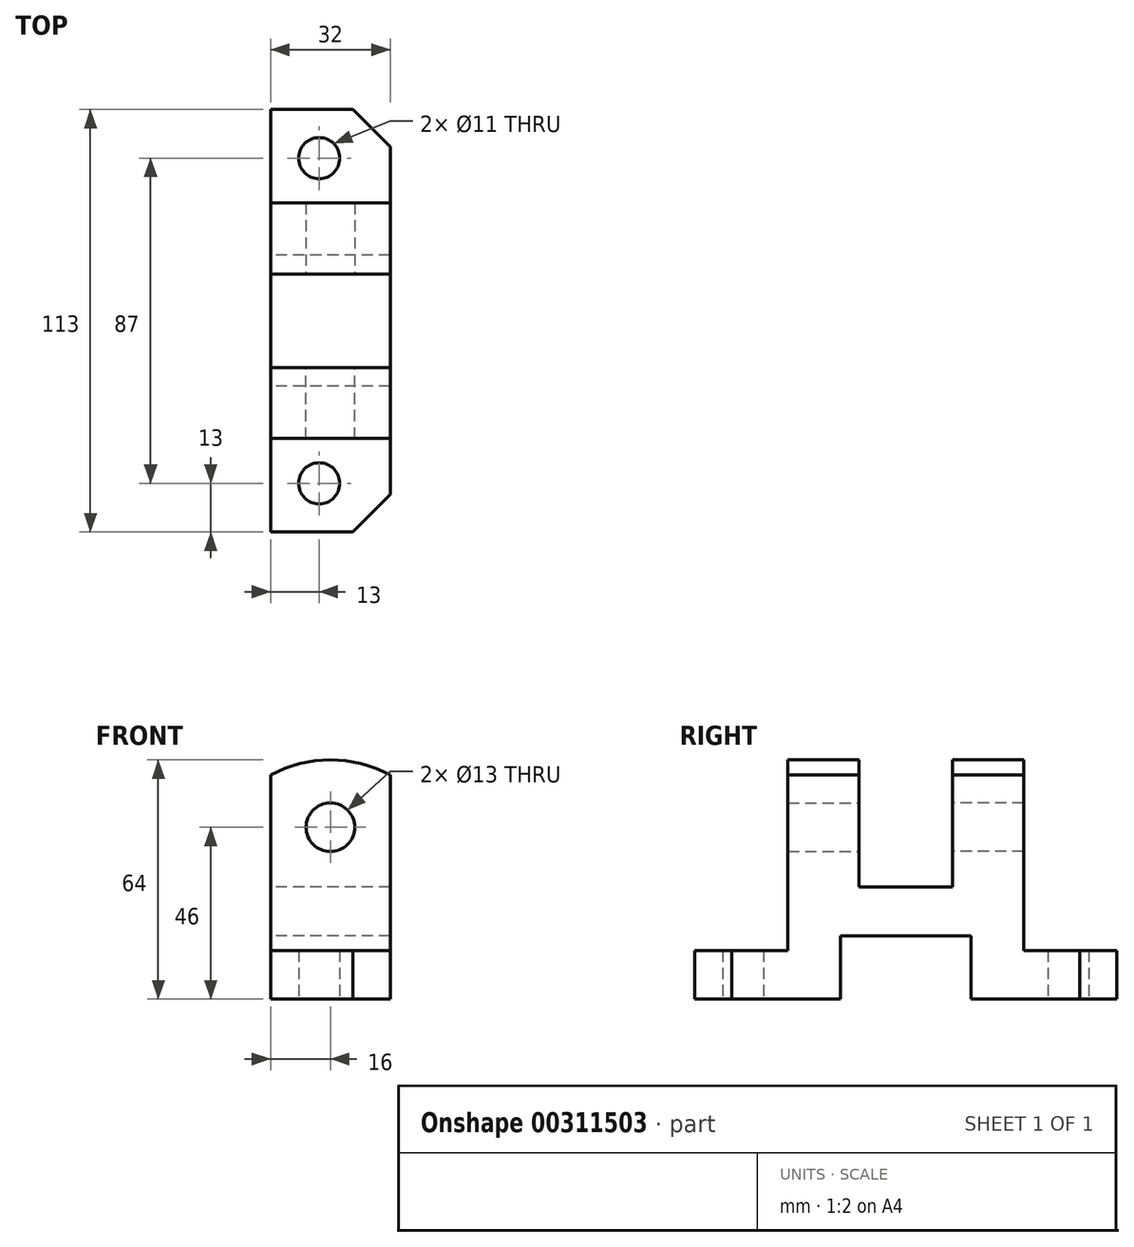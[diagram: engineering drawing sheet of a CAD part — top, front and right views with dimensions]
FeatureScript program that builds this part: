
annotation { "Feature Type Name" : "Feature", "Feature Type Description" : "" }
export const myFeature = defineFeature(function(context is Context, id is Id, definition is map)
    precondition{}
    {
        {
            var Q0;
            Q0=qCreatedBy(makeId("Front.planeOp"),FACE);
            var sketch = newSketch(context, id + "F0", { "sketchPlane" : qUnion([Q0])});
            skLineSegment(sketch, "E0", {"start": v(0, 0) * mm, "end": v(0, 30) * mm});
            skLineSegment(sketch, "E1", {"start": v(0, 30) * mm, "end": v(32, 30) * mm, "construction": true});
            skLineSegment(sketch, "E2", {"start": v(32, 30) * mm, "end": v(32, 0) * mm});
            skLineSegment(sketch, "E3", {"start": v(32, 0) * mm, "end": v(0, 0) * mm});
            skCircle(sketch, "E4", {"center": v(16, 16) * mm, "radius": 6.5 * mm});
            skArc(sketch, "E5", {"start": v(32, 30) * mm, "mid": v(16, 34) * mm, "end": v(0, 30) * mm});
            skSolve(sketch);
        }
        {
            var Q0;
            Q0 = qSketchRegion(id + "F0", true);
            extrude(context, id + "F1", {"entities" : qUnion([Q0]), "depth" : 19 * mm});
        }
        {
            var Q0;
            Q0=makeQuery(id+"F1.opExtrude","CAP_FACE",FACE,{"disambiguationData":[OSD([sQuery(id+"F0.wireOp",EDGE,"E0"),sQuery(id+"F0.wireOp",EDGE,"E2"),sQuery(id+"F0.wireOp",EDGE,"E3"),sQuery(id+"F0.wireOp",EDGE,"E4"),sQuery(id+"F0.wireOp",EDGE,"E5")])],"isStart":true});
            var sketch = newSketch(context, id + "F2", { "sketchPlane" : qUnion([Q0])});
            skLineSegment(sketch, "E6", {"start": v(0, 0) * mm, "end": v(-32, 0) * mm});
            skLineSegment(sketch, "E7", {"start": v(-32, 0) * mm, "end": v(-32, -13) * mm});
            skLineSegment(sketch, "E8", {"start": v(-32, -13) * mm, "end": v(0, -13) * mm});
            skLineSegment(sketch, "E9", {"start": v(0, -13) * mm, "end": v(0, 0) * mm});
            skSolve(sketch);
        }
        {
            var Q0;
            Q0 = qSketchRegion(id + "F2", true);
            extrude(context, id + "F3", {"entities" : qUnion([Q0]), "depth" : 12.5 * mm, "hasSecondDirection" : true, "secondDirectionOppositeDirection" : true, "secondDirectionDepth" : 19 * mm});
        }
        {
            var Q0;
            Q0=makeQuery(id+"F3.opExtrude","SWEPT_FACE",FACE,{"disambiguationData":[OSD([sQuery(id+"F2.wireOp",EDGE,"E8")])]});
            var sketch = newSketch(context, id + "F4", { "sketchPlane" : qUnion([Q0])});
            skLineSegment(sketch, "E10", {"start": v(0, 19) * mm, "end": v(32, 19) * mm});
            skLineSegment(sketch, "E11", {"start": v(32, 19) * mm, "end": v(32, 5) * mm});
            skLineSegment(sketch, "E12", {"start": v(32, 5) * mm, "end": v(0, 5) * mm});
            skLineSegment(sketch, "E13", {"start": v(0, 5) * mm, "end": v(0, 19) * mm});
            skSolve(sketch);
        }
        {
            var Q0;
            Q0 = qSketchRegion(id + "F4", true);
            extrude(context, id + "F5", {"entities" : qUnion([Q0]), "operationType" : NewBodyOperationType.ADD, "depth" : 17 * mm});
        }
        {
            var Q0;
            Q0=qCreatedBy(makeId("Top.planeOp"),FACE);
            cPlane(context, id + "F6", {"entities" : qUnion([Q0]), "cplaneType" : CPlaneType.OFFSET, "offset" : 30 * mm, "oppositeDirection" : true, "width" : 150 * mm, "height" : 150 * mm});
        }
        {
            var Q0;
            Q0=qCreatedBy(id+"F6.planeOp",FACE);
            var sketch = newSketch(context, id + "F7", { "sketchPlane" : qUnion([Q0])});
            skLineSegment(sketch, "E14", {"start": v(0, -19) * mm, "end": v(0, -44) * mm});
            skLineSegment(sketch, "E15", {"start": v(0, -44) * mm, "end": v(22, -44) * mm});
            skLineSegment(sketch, "E16", {"start": v(22, -44) * mm, "end": v(32, -34) * mm});
            skLineSegment(sketch, "E17", {"start": v(32, -34) * mm, "end": v(32, -19) * mm});
            skLineSegment(sketch, "E18", {"start": v(32, -19) * mm, "end": v(0, -19) * mm});
            skCircle(sketch, "E19", {"center": v(13, -31) * mm, "radius": 5.5 * mm});
            skSolve(sketch);
        }
        {
            var Q0;
            Q0 = qSketchRegion(id + "F7", true);
            extrude(context, id + "F8", {"entities" : qUnion([Q0]), "operationType" : NewBodyOperationType.ADD, "depth" : 13 * mm});
        }
        {
            var Q0;
            Q0=qCreatedBy(makeId("Front.planeOp"),FACE);
            cPlane(context, id + "F9", {"entities" : qUnion([Q0]), "cplaneType" : CPlaneType.OFFSET, "offset" : 12.5 * mm, "oppositeDirection" : true, "width" : 150 * mm, "height" : 150 * mm});
        }
        {
            var Q0;
            Q0=makeQuery(id+"F1.opExtrude","SWEPT_BODY",BODY,{"disambiguationData":[OSD([sQuery(id+"F0.wireOp",EDGE,"E0"),sQuery(id+"F0.wireOp",EDGE,"E2"),sQuery(id+"F0.wireOp",EDGE,"E3"),sQuery(id+"F0.wireOp",EDGE,"E4"),sQuery(id+"F0.wireOp",EDGE,"E5")])]});
            var Q1;
            Q1=makeQuery(id+"F3.opExtrude","SWEPT_BODY",BODY,{"disambiguationData":[OSD([sQuery(id+"F2.wireOp",EDGE,"E6"),sQuery(id+"F2.wireOp",EDGE,"E7"),sQuery(id+"F2.wireOp",EDGE,"E8"),sQuery(id+"F2.wireOp",EDGE,"E9")])]});
            var Q2;
            Q2=qCreatedBy(id+"F9.planeOp",FACE);
            mirror(context, id + "F10", {"operationType" : NewBodyOperationType.ADD, "entities" : qUnion([Q0, Q1]), "mirrorPlane" : qUnion([Q2])});
        }
    });
